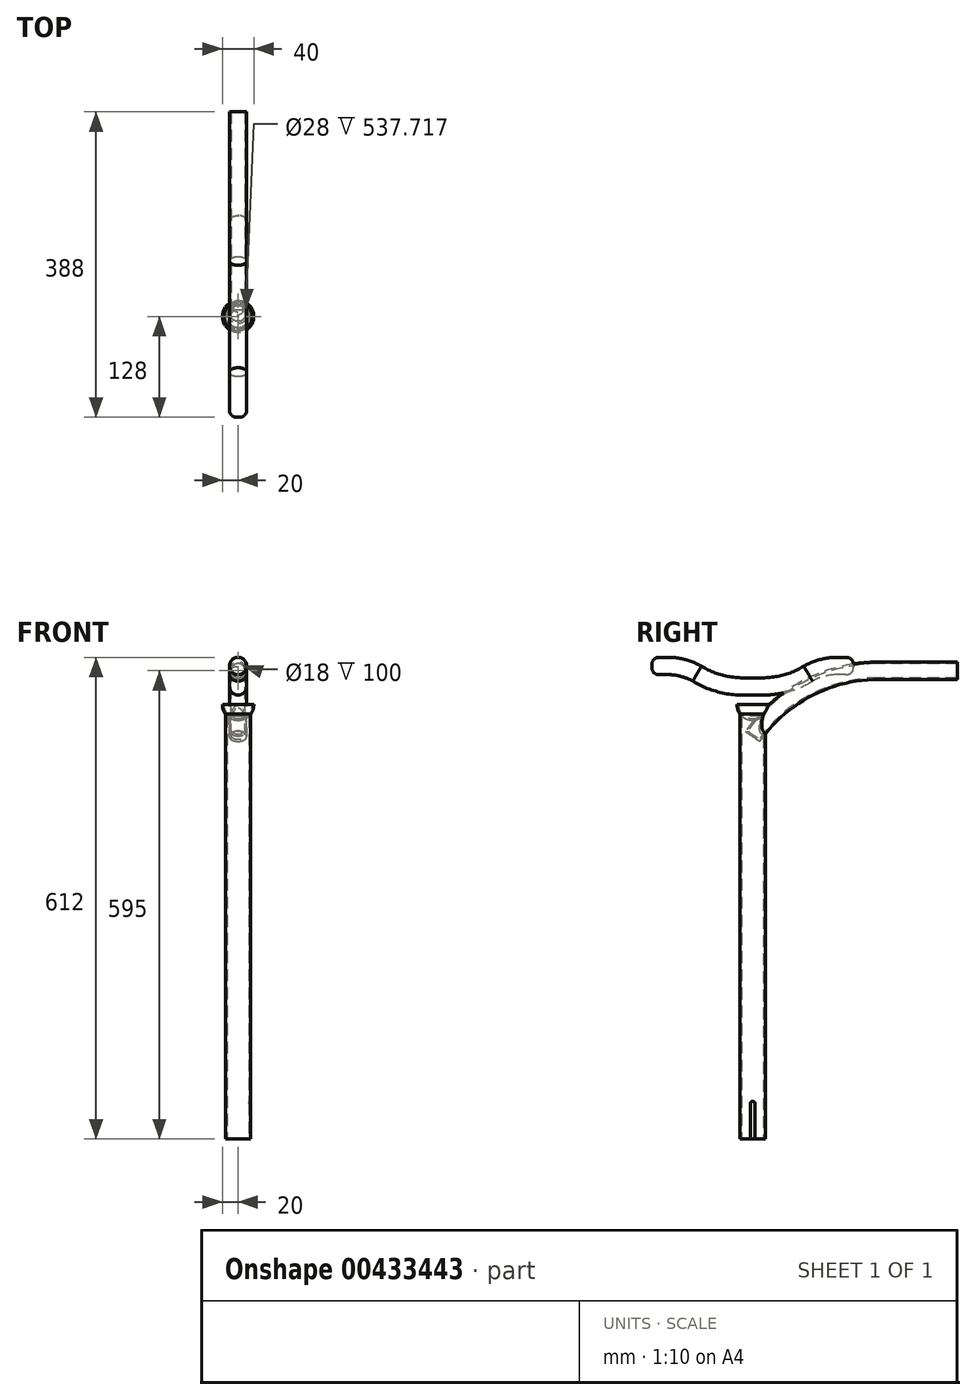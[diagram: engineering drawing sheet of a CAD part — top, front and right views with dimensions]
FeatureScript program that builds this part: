
annotation { "Feature Type Name" : "Feature", "Feature Type Description" : "" }
export const myFeature = defineFeature(function(context is Context, id is Id, definition is map)
    precondition{}
    {
        {
            var Q0;
            Q0=qCreatedBy(makeId("Top.planeOp"),FACE);
            var sketch = newSketch(context, id + "F0", { "sketchPlane" : qUnion([Q0])});
            skCircle(sketch, "E0", {"center": v(0, 0) * mm, "radius": 16 * mm});
            skSolve(sketch);
        }
        {
            var Q0;
            Q0=makeQuery(id+"F0.imprint","IMPRINT",FACE,{"disambiguationData":[TD([[makeQuery(id+"F0.imprint","IMPRINT",EDGE,{"derivedFrom":sQuery(id+"F0.wireOp",EDGE,"E0")}),1.0]])]});
            extrude(context, id + "F1", {"entities" : qUnion([Q0]), "depth" : 550 * mm});
        }
        {
            var Q0;
            Q0=makeQuery(id+"F1.opExtrude","CAP_FACE",FACE,{"disambiguationData":[OSD([sQuery(id+"F0.wireOp",EDGE,"E0")])],"isStart":true});
            shell(context, id + "F2", {"entities" : qUnion([Q0]), "thickness" : 2 * mm});
        }
        {
            var Q0;
            Q0=qCreatedBy(makeId("Right.planeOp"),FACE);
            var sketch = newSketch(context, id + "F3", { "sketchPlane" : qUnion([Q0])});
            skLineSegment(sketch, "E1.bottom", {"start": v(-3, 0) * mm, "end": v(3, 0) * mm});
            skLineSegment(sketch, "E1.left", {"start": v(-3, 0) * mm, "end": v(-3, 45) * mm});
            skLineSegment(sketch, "E1.right", {"start": v(3, 0) * mm, "end": v(3, 45) * mm});
            skArc(sketch, "E2", {"start": v(3, 45) * mm, "mid": v(0, 48) * mm, "end": v(-3, 45) * mm});
            skSolve(sketch);
        }
        {
            var Q0;
            Q0=qSketchRegion(id+"F3",true);
            extrude(context, id + "F4", {"entities" : qUnion([Q0]), "operationType" : NewBodyOperationType.REMOVE, "endBound" : BoundingType.THROUGH_ALL, "depth" : 25 * mm});
        }
        {
            var Q0;
            Q0=qCreatedBy(makeId("Right.planeOp"),FACE);
            var sketch = newSketch(context, id + "F5", { "sketchPlane" : qUnion([Q0])});
            skArc(sketch, "E3", {"start": v(160, 595) * mm, "mid": v(69.75, 572.86) * mm, "end": v(0, 511.47) * mm});
            skLineSegment(sketch, "E4", {"start": v(160, 595) * mm, "end": v(260, 595) * mm});
            skSolve(sketch);
        }
        {
            var Q0;
            Q0=sQuery(id+"F5.wireOp",VERTEX,"E4.end");
            var Q1;
            Q1=qCreatedBy(makeId("Front.planeOp"),FACE);
            cPlane(context, id + "F6", {"entities" : qUnion([Q0, Q1]), "cplaneType" : CPlaneType.PLANE_POINT, "offset" : 25 * mm, "width" : 150 * mm, "height" : 150 * mm});
        }
        {
            var Q0;
            Q0=qCreatedBy(id+"F6.planeOp",FACE);
            var sketch = newSketch(context, id + "F7", { "sketchPlane" : qUnion([Q0])});
            skCircle(sketch, "E5", {"center": v(0, 595) * mm, "radius": 11 * mm});
            skSolve(sketch);
        }
        {
            var Q0;
            Q0=makeQuery(id+"F7.imprint","IMPRINT",FACE,{"disambiguationData":[TD([[makeQuery(id+"F7.imprint","IMPRINT",EDGE,{"derivedFrom":sQuery(id+"F7.wireOp",EDGE,"E5")}),1.0]])]});
            var Q1;
            Q1=qConstructionFilter(qBodyType(qCreatedBy(id+"F5",EDGE),BodyType.WIRE),ConstructionObject.NO);
            sweep(context, id + "F8", {"operationType" : NewBodyOperationType.ADD, "profiles" : qUnion([Q0]), "path" : qUnion([Q1])});
        }
        {
            var Q0;
            Q0=makeQuery(id+"F8.opSweep","CAP_FACE",FACE,{"disambiguationData":[OSD([sQuery(id+"F5.wireOp",VERTEX,"E4.end"),sQuery(id+"F7.wireOp",EDGE,"E5")])],"isStart":true});
            shell(context, id + "F9", {"entities" : qUnion([Q0]), "thickness" : 2 * mm});
        }
        {
            var Q0;
            Q0=qCreatedBy(makeId("Right.planeOp"),FACE);
            var sketch = newSketch(context, id + "F10", { "sketchPlane" : qUnion([Q0])});
            skLineSegment(sketch, "E6", {"start": v(-128, 601) * mm, "end": v(-108, 601) * mm});
            skArc(sketch, "E7", {"start": v(-70.5, 591.19) * mm, "mid": v(-88.62, 598.5) * mm, "end": v(-108, 601) * mm});
            skArc(sketch, "E8", {"start": v(-70.5, 591.19) * mm, "mid": v(-42.6, 579.12) * mm, "end": v(-12.5, 575) * mm});
            skLineSegment(sketch, "E9", {"start": v(-12.5, 575) * mm, "end": v(0, 575) * mm});
            skLineSegment(sketch, "E10", {"start": v(0, 0) * mm, "end": v(0, 575) * mm, "construction": true});
            skArc(sketch, "E11.MirrorCS", {"start": v(70.5, 591.19) * mm, "mid": v(42.6, 579.12) * mm, "end": v(12.5, 575) * mm});
            skLineSegment(sketch, "E12.MirrorCS", {"start": v(12.5, 575) * mm, "end": v(0, 575) * mm});
            skArc(sketch, "E13.MirrorCS", {"start": v(70.5, 591.19) * mm, "mid": v(88.62, 598.5) * mm, "end": v(108, 601) * mm});
            skLineSegment(sketch, "E14.MirrorCS", {"start": v(128, 601) * mm, "end": v(108, 601) * mm});
            skSolve(sketch);
        }
        {
            var Q0;
            Q0=sQuery(id+"F10.wireOp",VERTEX,"E14.MirrorCS.start");
            var Q1;
            Q1=qCreatedBy(id+"F6.planeOp",FACE);
            cPlane(context, id + "F11", {"entities" : qUnion([Q0, Q1]), "cplaneType" : CPlaneType.PLANE_POINT, "offset" : 25 * mm, "width" : 150 * mm, "height" : 150 * mm});
        }
        {
            var Q0;
            Q0=qCreatedBy(id+"F11.planeOp",FACE);
            var sketch = newSketch(context, id + "F12", { "sketchPlane" : qUnion([Q0])});
            skCircle(sketch, "E15", {"center": v(0, 601) * mm, "radius": 11 * mm});
            skSolve(sketch);
        }
        {
            var Q0;
            Q0=qSketchRegion(id+"F12",true);
            var Q1;
            Q1=qConstructionFilter(qBodyType(qCreatedBy(id+"F10",EDGE),BodyType.WIRE),ConstructionObject.NO);
            sweep(context, id + "F13", {"profiles" : qUnion([Q0]), "path" : qUnion([Q1])});
        }
        {
            var Q0;
            Q0=makeQuery(id+"F13.opSweep","CAP_EDGE",EDGE,{"disambiguationData":[OSD([sQuery(id+"F10.wireOp",VERTEX,"E6.start"),sQuery(id+"F12.wireOp",EDGE,"E15")])],"isStart":false});
            var Q1;
            Q1=makeQuery(id+"F13.opSweep","CAP_EDGE",EDGE,{"disambiguationData":[OSD([sQuery(id+"F10.wireOp",VERTEX,"E14.MirrorCS.start"),sQuery(id+"F12.wireOp",EDGE,"E15")])],"isStart":true});
            fillet(context, id + "F14", {"entities" : qUnion([Q0, Q1]), "radius" : 10 * mm, "tangentPropagation" : true, "rho" : .5, "crossSection" : FilletCrossSection.CONIC, "allowEdgeOverflow" : false});
        }
        {
            var Q0;
            Q0=qCreatedBy(makeId("Right.planeOp"),FACE);
            var sketch = newSketch(context, id + "F15", { "sketchPlane" : qUnion([Q0])});
            skArc(sketch, "E16", {"start": v(-20, 551.93) * mm, "mid": v(-14.12, 537.83) * mm, "end": v(0, 532) * mm});
            skLineSegment(sketch, "E17", {"start": v(0, 532) * mm, "end": v(0, 552) * mm});
            skLineSegment(sketch, "E18", {"start": v(-20, 551.93) * mm, "end": v(0, 551.93) * mm});
            skPoint(sketch, "E19.orphan", {"position": v(0, 529.24) * mm});
            skSolve(sketch);
        }
        {
            var Q0;
            Q0=qSketchRegion(id+"F15",true);
            var Q1;
            Q1=sQuery(id+"F15.wireOp",EDGE,"E17");
            revolve(context, id + "F16", {"operationType" : NewBodyOperationType.ADD, "entities" : qUnion([Q0]), "axis" : qUnion([Q1]), "revolveType" : RevolveType.FULL});
        }
        {
            var Q0;
            Q0=makeQuery(id+"F16.opRevolve","SWEPT_FACE",FACE,{"disambiguationData":[OSD([sQuery(id+"F15.wireOp",EDGE,"E18")])]});
            shell(context, id + "F17", {"entities" : qUnion([Q0]), "thickness" : 2 * mm});
        }
    });
